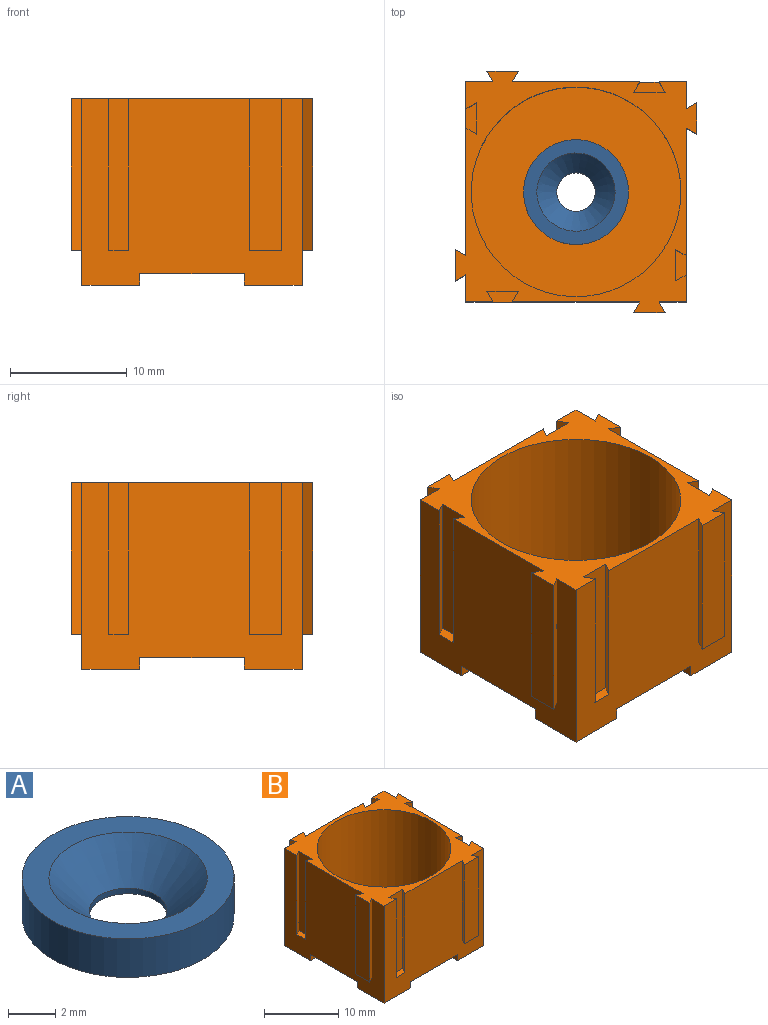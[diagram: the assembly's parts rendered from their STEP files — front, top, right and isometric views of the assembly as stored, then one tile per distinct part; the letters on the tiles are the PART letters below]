
ASSEMBLY  parts=2 mates=1
PART A: 5 faces, bbox 9x9x2 mm
  f0: cylinder r=4.5mm len=9mm, axis (0,0,-1), area 56.5mm2, adj f1,f2
  f1: plane 9x9mm, normal (0,0,1), area 28.1mm2, adj f0,f4
  f2: plane 9x9mm, normal (0,0,-1), area 55.1mm2, adj f0,f3
  f3: cylinder r=1.65mm len=3.3mm, axis (0,0,1), area 3mm2, adj f2,f4
  f4: cone r=1.65mm half-angle=45deg, axis (0,0,1), area 38.1mm2, adj f1,f3
PART B: 53 faces, bbox 20.7x20.7x16 mm
  f0: plane 4.95x4.95mm, normal (0,0,-1), area 24.5mm2, adj f14,f21,f43,f44
  f1: plane 4.95x4.95mm, normal (0,0,-1), area 24.5mm2, adj f3,f4,f47,f48
  f2: plane 4.95x4.95mm, normal (0,0,-1), area 24.5mm2, adj f3,f21,f49,f50
  f3: plane 18.9x16mm, normal (-1,0,0), area 250.2mm2, adj f1,f2,f4,f7,f21,f22,f24,f25
  f4: plane 18.9x16mm, normal (0,-1,0), area 250.2mm2, adj f1,f3,f5,f14,f28,f30,f31,f33
  f5: plane 2.7x0.9mm, normal (0,0,-1), area 2mm2, adj f4,f31,f32,f33
  f6: plane 2.7x0.9mm, normal (0,0,-1), area 2mm2, adj f18,f19,f20,f21
  f7: plane 2.7x0.9mm, normal (0,0,-1), area 2mm2, adj f3,f25,f26,f27
  f8: plane 13x0.9mm, normal (-0.5,0.87,0), area 13.5mm2, adj f9,f14,f35,f42
  f9: plane 13x2.7mm, normal (1,0,0), area 35.1mm2, adj f8,f10,f35,f42
  f10: plane 13x0.9mm, normal (-0.5,-0.87,0), area 13.5mm2, adj f9,f14,f35,f42
  f11: plane 13x0.9mm, normal (-0.5,-0.87,0), area 13.5mm2, adj f12,f14,f35,f36
  f12: plane 13x2.7mm, normal (1,0,0), area 35.1mm2, adj f11,f13,f35,f36
  f13: plane 13x0.9mm, normal (-0.5,0.87,0), area 13.5mm2, adj f12,f14,f35,f36
  f14: plane 18.9x16mm, normal (1,0,0), area 250.2mm2, adj f0,f4,f8,f10,f11,f13,f21,f35
  f15: plane 13x0.9mm, normal (-0.87,-0.5,0), area 13.5mm2, adj f16,f21,f35,f40
  f16: plane 13x2.7mm, normal (0,1,0), area 35.1mm2, adj f15,f17,f35,f40
  f17: plane 13x0.9mm, normal (0.87,-0.5,0), area 13.5mm2, adj f16,f21,f35,f40
  f18: plane 13x0.9mm, normal (0.87,-0.5,0), area 13.5mm2, adj f6,f19,f21,f35
  f19: plane 13x2.7mm, normal (0,1,0), area 35.1mm2, adj f6,f18,f20,f35
  f20: plane 13x0.9mm, normal (-0.87,-0.5,0), area 13.5mm2, adj f6,f19,f21,f35
  f21: plane 18.9x16mm, normal (0,1,0), area 250.2mm2, adj f0,f2,f3,f6,f14,f15,f17,f18
  f22: plane 13x0.9mm, normal (0.5,-0.87,0), area 13.5mm2, adj f3,f23,f35,f39
  f23: plane 13x2.7mm, normal (-1,0,0), area 35.1mm2, adj f22,f24,f35,f39
  f24: plane 13x0.9mm, normal (0.5,0.87,0), area 13.5mm2, adj f3,f23,f35,f39
  f25: plane 13x0.9mm, normal (0.5,0.87,0), area 13.5mm2, adj f3,f7,f26,f35
  f26: plane 13x2.7mm, normal (-1,0,0), area 35.1mm2, adj f7,f25,f27,f35
  f27: plane 13x0.9mm, normal (0.5,-0.87,0), area 13.5mm2, adj f3,f7,f26,f35
  f28: plane 13x0.9mm, normal (0.87,0.5,0), area 13.5mm2, adj f4,f29,f35,f38
  f29: plane 13x2.7mm, normal (0,-1,0), area 35.1mm2, adj f28,f30,f35,f38
  f30: plane 13x0.9mm, normal (-0.87,0.5,0), area 13.5mm2, adj f4,f29,f35,f38
  f31: plane 13x0.9mm, normal (-0.87,0.5,0), area 13.5mm2, adj f4,f5,f32,f35
  f32: plane 13x2.7mm, normal (0,-1,0), area 35.1mm2, adj f5,f31,f33,f35
  f33: plane 13x0.9mm, normal (0.87,0.5,0), area 13.5mm2, adj f4,f5,f32,f35
  f34: cylinder r=9mm len=18mm, axis (0,0,-1), area 735.1mm2, adj f35,f37
  f35: plane 20.7x20.7mm, normal (0,0,1), area 102.7mm2, adj f3,f4,f8,f9,f10,f11,f12,f13
  f36: plane 2.7x0.9mm, normal (0,0,-1), area 2mm2, adj f11,f12,f13,f14
  f37: plane 18x18mm, normal (0,0,1), area 245.9mm2, adj f34,f52
  f38: plane 2.7x0.9mm, normal (0,0,1), area 2mm2, adj f4,f28,f29,f30
  f39: plane 2.7x0.9mm, normal (0,0,1), area 2mm2, adj f3,f22,f23,f24
  f40: plane 2.7x0.9mm, normal (0,0,1), area 2mm2, adj f15,f16,f17,f21
  f41: plane 4.95x4.95mm, normal (0,0,-1), area 24.5mm2, adj f4,f14,f45,f46
  f42: plane 2.7x0.9mm, normal (0,0,1), area 2mm2, adj f8,f9,f10,f14
  f43: plane 4.95x1mm, normal (-1,0,0), area 5mm2, adj f0,f21,f44,f51
  f44: plane 4.95x1mm, normal (0,-1,0), area 5mm2, adj f0,f14,f43,f51
  f45: plane 4.95x1mm, normal (0,1,0), area 5mm2, adj f14,f41,f46,f51
  f46: plane 4.95x1mm, normal (-1,0,0), area 5mm2, adj f4,f41,f45,f51
  f47: plane 4.95x1mm, normal (1,0,0), area 5mm2, adj f1,f4,f48,f51
  f48: plane 4.95x1mm, normal (0,1,0), area 5mm2, adj f1,f3,f47,f51
  f49: plane 4.95x1mm, normal (0,-1,0), area 5mm2, adj f2,f3,f50,f51
  f50: plane 4.95x1mm, normal (1,0,0), area 5mm2, adj f2,f21,f49,f51
  f51: plane 18.9x18.9mm, normal (0,0,-1), area 250.6mm2, adj f3,f4,f14,f21,f43,f44,f45,f46
  f52: cylinder r=1.65mm len=3.3mm, axis (0,0,1), area 20.7mm2, adj f37,f51
PLACE A t=(0.12,0.1,-4.96)mm
PLACE B t=(0.12,0.1,-4.96)mm fixed
MATE fastened A.f0 <-> B.f34  axis (0,0,-1) through (0.12,0.1,-4.96)mm
